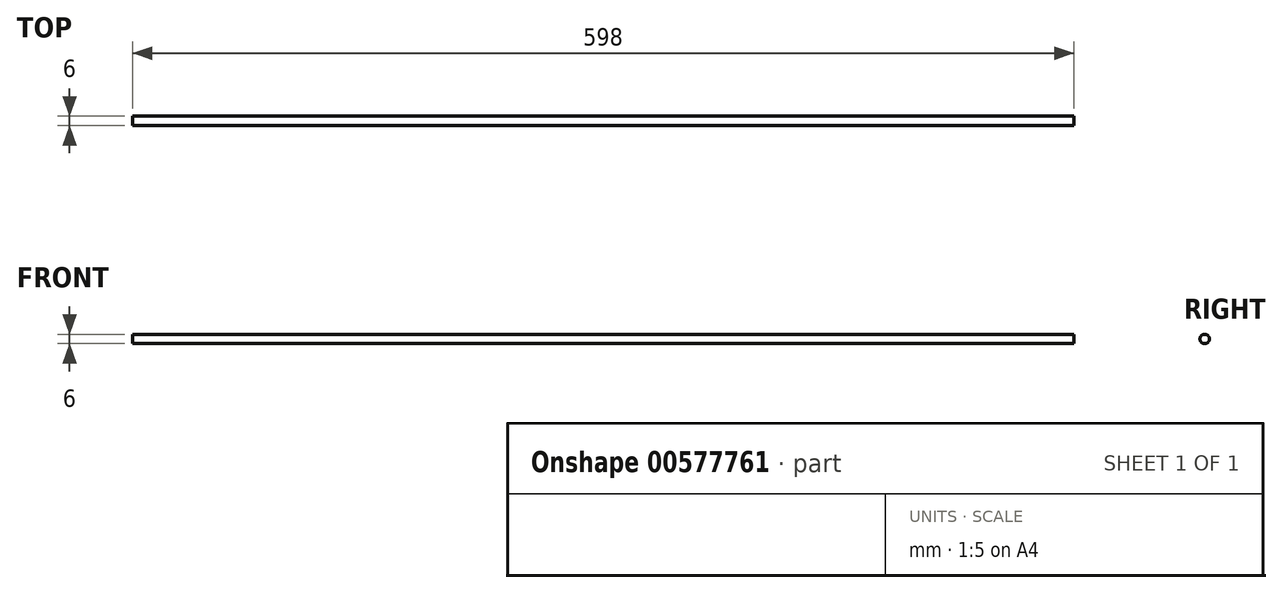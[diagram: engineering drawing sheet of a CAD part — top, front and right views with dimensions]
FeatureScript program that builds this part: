
annotation { "Feature Type Name" : "Feature", "Feature Type Description" : "" }
export const myFeature = defineFeature(function(context is Context, id is Id, definition is map)
    precondition{}
    {
        {
            var Q0;
            Q0=qCreatedBy(makeId("Right.planeOp"),FACE);
            var sketch = newSketch(context, id + "F0", { "sketchPlane" : qUnion([Q0])});
            skCircle(sketch, "E0", {"center": v(0, 0) * mm, "radius": 3 * mm});
            skSolve(sketch);
        }
        {
            var Q0;
            Q0 = qSketchRegion(id + "F0", true);
            extrude(context, id + "F1", {"entities" : qUnion([Q0]), "endBound" : BoundingType.SYMMETRIC, "depth" : 598 * mm, "offsetDistance" : 25 * mm});
        }
    });
